# Revit family: Haworth_BeHold_Bookcase
name_source: partatom
category: Furniture Systems
revit_build: Autodesk Revit 2018 (Build: 20170223_1515(x64)
units: mm (PartAtom-declared; Revit-internal decimal feet)

## family parameters
Always vertical = Yes
Cut with Voids When Loaded = No
OmniClass Number = 23.40.70.14.64.21
OmniClass Title = Systems Furniture
Part Type = Normal
Room Calculation Point = No
Round Connector Dimension = Use Diameter
Shared = No
Work Plane-Based = No

## types (5) — shared parameters
16in. Depth = No
24in. Depth = Yes
Actual Depth = 24 "
Actual Shelf 1 = Yes
Actual Shelf 2 = Yes
Actual Width = 36 "
Assembly Code = E2020200
Base Height = 0.75 "
Custom Size = No
Description = Haworth - Be_Hold - Freestanding Storage - Freestanding Bookcase
Inset Style = Yes
Inset Style Width = 23.81 "
Manufacturer = Haworth
Max. Height = 81 "
Max. Width = 36 "
Min. Height = 49 "
Min. Width = 18 "
Model = Haworth Be_Hold
Mounting Height = 22 "
Panel Thickness = 0.75 "
Proud Style = No
Revision Number = 1
Shelf Depth = 23.25 "
Shelf Height 1 = 14.94 "
Shelf Height 2 = 15.25 "
Shelf Height 4 = 15.25 "
Shelf Height 5 = 15.25 "
Shelf Width = 34.5 "
Side Case Back Control = 24 "
Size = Verify Final Dim. w/ Haworth
Standard Depths = 16, 24 in
Standard Height = 49-81 in.
Standard Widths = 18-36 in. @ 6 in. increments
Sustainability Info = https://www.haworth.com
URL = www.haworth.com
URL - Product = https://www.haworth.com
Width = 36 "
zero-valued in all types: Back Case Back Control, Back Case Side Control

## per-type parameters (varying)
| type | Actual Height | Actual Shelf 3 | Actual Shelf 4 | Height | Shelf Height 3 |
| 49h 36w | 49 " | No | No | 49 " | 15.25 " |
| 65h 36w | 65 " | Yes | No | 65 " | 15.25 " |
| 57h 36w | 57 " | Yes | No | 57 " | 7.25 " |
| 73h 36w | 73 " | Yes | Yes | 73 " | 7.25 " |
| 81h 36w | 81 " | Yes | Yes | 81 " | 15.25 " |

## geometry (parser evidence)
native form markers: Sweep x5
no freeform markers — native parametric forms only
